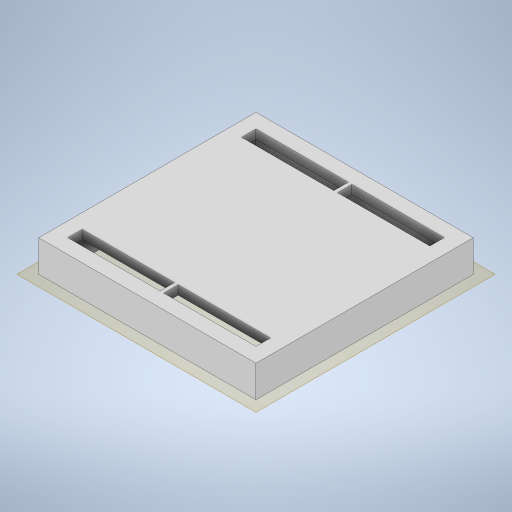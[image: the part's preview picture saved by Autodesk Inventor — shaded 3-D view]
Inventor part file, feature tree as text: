
AUTODESK INVENTOR PART (.ipt)
format: ipt  version: 2024 (Build 280153000, 153)  size: 307,712 bytes
history: native  units: in
note: dims shown in document units (in); Inventor stores cm internally (conversion verified against a paired STEP export)
features: extrude x4, sketch x4, projected_geometry x2, plane x1, mirror x1
ambient origin geometry x8: Origin, YZ Plane, XZ Plane, XY Plane, X Axis, Y Axis, Z Axis, Center Point
bodies: Solid1 (feature_tree)
feature tree (12):
  extrude  "Extrusion1"  Depth=6.0in
  extrude  "Extrusion2"  Depth=0.4in
  extrude  "Extrusion3"  Depth=0.4in
  plane  "Work Plane1"
  mirror  "Mirror1"
  extrude  "Extrusion4"  Depth=2.55in
  sketch  "Sketch1"  dims[d0=6.0in d1=6.0in]
  sketch  "Sketch2"  dims[d2=0.25in d3=0.0in d4=0.4in]
  sketch  "Sketch3"  dims[d5=0.4in d6=0.4in]
  projected_geometry  "Projected Loop1"
  sketch  "Sketch5"  dims[d7=2.55in d8=2.55in d9=0.4in d10=0.4in d11=0.4in d12=0.0in d13=0.0in d14=0.25in d15=1.5in d16=0.0in d17=0.0in d18=0.0in]
  projected_geometry  "Projected Loop2"
